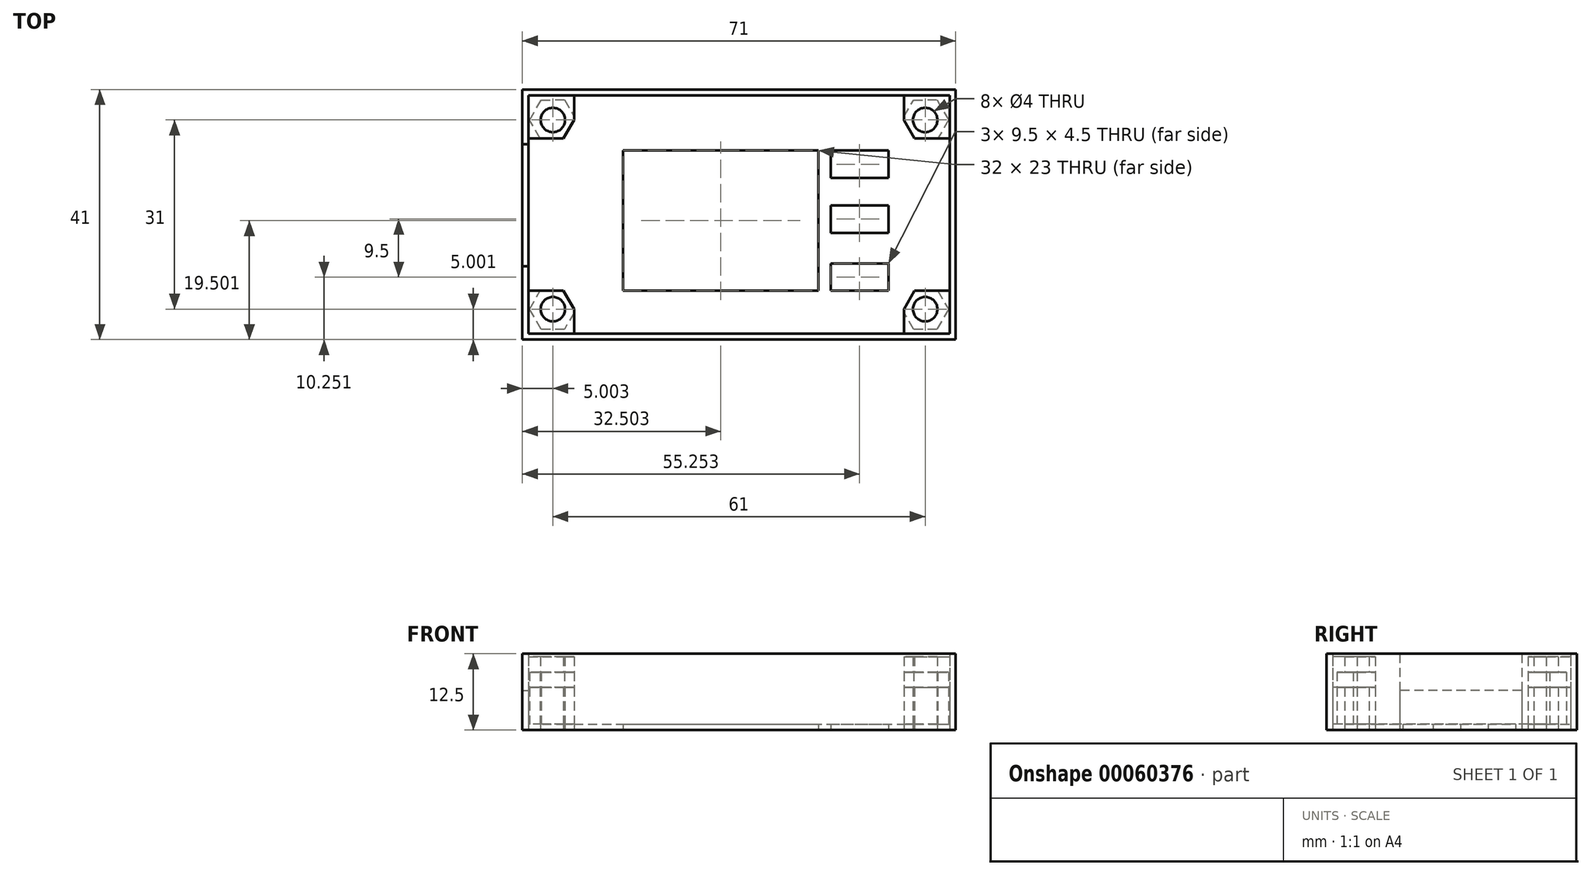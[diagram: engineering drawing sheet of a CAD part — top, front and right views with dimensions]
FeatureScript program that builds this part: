
annotation { "Feature Type Name" : "Feature", "Feature Type Description" : "" }
export const myFeature = defineFeature(function(context is Context, id is Id, definition is map)
    precondition{}
    {
        {
            var Q0;
            Q0=qCreatedBy(makeId("Top.planeOp"),FACE);
            var sketch = newSketch(context, id + "F0", { "sketchPlane" : qUnion([Q0])});
            skCircle(sketch, "E0.cCircle", {"center": v(0, 0) * mm, "radius": 3 * mm, "construction": true});
            skLineSegment(sketch, "E0.0", {"start": v(1.73, 3) * mm, "end": v(3.46, 0) * mm});
            skLineSegment(sketch, "E0.1", {"start": v(3.46, 0) * mm, "end": v(1.74, -3) * mm});
            skLineSegment(sketch, "E0.2", {"start": v(1.74, -3) * mm, "end": v(-1.73, -3) * mm});
            skLineSegment(sketch, "E0.3", {"start": v(-1.73, -3) * mm, "end": v(-3.46, 0) * mm});
            skLineSegment(sketch, "E0.4", {"start": v(-3.46, 0) * mm, "end": v(-1.74, 3) * mm});
            skLineSegment(sketch, "E0.5", {"start": v(-1.74, 3) * mm, "end": v(1.73, 3) * mm});
            skPoint(sketch, "E0.0.midPoint", {"position": v(2.6, 1.5) * mm});
            skCircle(sketch, "E1", {"center": v(0, 0) * mm, "radius": 1.5 * mm});
            skLineSegment(sketch, "E2.bottom", {"start": v(-12.76, 68.41) * mm, "end": v(56.24, 68.41) * mm});
            skLineSegment(sketch, "E2.top", {"start": v(-12.76, 29.41) * mm, "end": v(56.24, 29.41) * mm});
            skLineSegment(sketch, "E2.left", {"start": v(-12.76, 68.41) * mm, "end": v(-12.76, 29.41) * mm});
            skLineSegment(sketch, "E2.right", {"start": v(56.24, 68.41) * mm, "end": v(56.24, 29.41) * mm});
            skPoint(sketch, "E3.0.midPoint", {"position": v(-6.16, 65.92) * mm});
            skLineSegment(sketch, "E3.3", {"start": v(-10.48, 61.4) * mm, "end": v(-12.22, 64.4) * mm, "construction": true});
            skLineSegment(sketch, "E3.2", {"start": v(-7.02, 61.41) * mm, "end": v(-10.48, 61.4) * mm});
            skLineSegment(sketch, "E3.1", {"start": v(-5.3, 64.42) * mm, "end": v(-7.02, 61.41) * mm});
            skLineSegment(sketch, "E3.0", {"start": v(-7.03, 67.41) * mm, "end": v(-5.3, 64.42) * mm, "construction": true});
            skLineSegment(sketch, "E3.4", {"start": v(-12.22, 64.4) * mm, "end": v(-10.5, 67.4) * mm, "construction": true});
            skLineSegment(sketch, "E3.5", {"start": v(-10.5, 67.4) * mm, "end": v(-7.03, 67.41) * mm, "construction": true});
            skCircle(sketch, "E4", {"center": v(-8.76, 64.41) * mm, "radius": 1.5 * mm, "construction": true});
            skCircle(sketch, "E3.cCircle", {"center": v(-8.76, 64.41) * mm, "radius": 3 * mm, "construction": true});
            skPoint(sketch, "E5.0.midPoint", {"position": v(-6.16, 34.92) * mm});
            skLineSegment(sketch, "E5.3", {"start": v(-10.48, 30.4) * mm, "end": v(-12.22, 33.4) * mm, "construction": true});
            skLineSegment(sketch, "E5.2", {"start": v(-7.02, 30.41) * mm, "end": v(-10.48, 30.4) * mm, "construction": true});
            skLineSegment(sketch, "E5.1", {"start": v(-5.3, 33.42) * mm, "end": v(-7.02, 30.41) * mm, "construction": true});
            skLineSegment(sketch, "E5.0", {"start": v(-7.03, 36.41) * mm, "end": v(-5.3, 33.42) * mm});
            skLineSegment(sketch, "E5.4", {"start": v(-12.22, 33.4) * mm, "end": v(-10.5, 36.4) * mm, "construction": true});
            skLineSegment(sketch, "E5.5", {"start": v(-10.5, 36.4) * mm, "end": v(-7.03, 36.41) * mm});
            skCircle(sketch, "E6", {"center": v(-8.76, 33.41) * mm, "radius": 1.5 * mm, "construction": true});
            skCircle(sketch, "E5.cCircle", {"center": v(-8.76, 33.41) * mm, "radius": 3 * mm, "construction": true});
            skPoint(sketch, "E7.0.midPoint", {"position": v(54.84, 65.92) * mm});
            skLineSegment(sketch, "E7.3", {"start": v(50.52, 61.4) * mm, "end": v(48.78, 64.4) * mm});
            skLineSegment(sketch, "E7.2", {"start": v(53.98, 61.41) * mm, "end": v(50.52, 61.4) * mm});
            skLineSegment(sketch, "E7.1", {"start": v(55.7, 64.42) * mm, "end": v(53.98, 61.41) * mm, "construction": true});
            skLineSegment(sketch, "E7.0", {"start": v(53.97, 67.41) * mm, "end": v(55.7, 64.42) * mm, "construction": true});
            skLineSegment(sketch, "E7.4", {"start": v(48.78, 64.4) * mm, "end": v(50.5, 67.4) * mm, "construction": true});
            skLineSegment(sketch, "E7.5", {"start": v(50.5, 67.4) * mm, "end": v(53.97, 67.41) * mm, "construction": true});
            skCircle(sketch, "E8", {"center": v(52.24, 64.41) * mm, "radius": 1.5 * mm, "construction": true});
            skCircle(sketch, "E7.cCircle", {"center": v(52.24, 64.41) * mm, "radius": 3 * mm, "construction": true});
            skPoint(sketch, "E9.0.midPoint", {"position": v(54.84, 34.92) * mm});
            skLineSegment(sketch, "E9.3", {"start": v(50.52, 30.4) * mm, "end": v(48.78, 33.4) * mm, "construction": true});
            skLineSegment(sketch, "E9.2", {"start": v(53.98, 30.41) * mm, "end": v(50.52, 30.4) * mm, "construction": true});
            skLineSegment(sketch, "E9.1", {"start": v(55.7, 33.42) * mm, "end": v(53.98, 30.41) * mm, "construction": true});
            skLineSegment(sketch, "E9.0", {"start": v(53.97, 36.41) * mm, "end": v(55.7, 33.42) * mm, "construction": true});
            skLineSegment(sketch, "E9.4", {"start": v(48.78, 33.4) * mm, "end": v(50.5, 36.4) * mm});
            skLineSegment(sketch, "E9.5", {"start": v(50.5, 36.4) * mm, "end": v(53.97, 36.41) * mm});
            skCircle(sketch, "E10", {"center": v(52.24, 33.41) * mm, "radius": 1.5 * mm, "construction": true});
            skCircle(sketch, "E9.cCircle", {"center": v(52.24, 33.41) * mm, "radius": 3 * mm, "construction": true});
            skLineSegment(sketch, "E11", {"start": v(48.78, 33.4) * mm, "end": v(48.78, 29.41) * mm});
            skLineSegment(sketch, "E12", {"start": v(53.97, 36.41) * mm, "end": v(56.24, 36.41) * mm});
            skCircle(sketch, "E13.0", {"center": v(52.24, 33.41) * mm, "radius": 2 * mm});
            skLineSegment(sketch, "E14.0", {"start": v(50.34, 30.1) * mm, "end": v(48.52, 33.25) * mm});
            skLineSegment(sketch, "E14.1", {"start": v(54.15, 30.11) * mm, "end": v(50.34, 30.1) * mm});
            skLineSegment(sketch, "E14.2", {"start": v(56.05, 33.42) * mm, "end": v(54.15, 30.11) * mm});
            skLineSegment(sketch, "E14.3", {"start": v(54.23, 36.56) * mm, "end": v(56.05, 33.42) * mm});
            skLineSegment(sketch, "E15", {"start": v(-5.3, 33.42) * mm, "end": v(-5.3, 29.41) * mm});
            skLineSegment(sketch, "E16", {"start": v(-10.5, 36.4) * mm, "end": v(-12.76, 36.4) * mm});
            skLineSegment(sketch, "E17", {"start": v(-10.48, 61.4) * mm, "end": v(-12.76, 61.4) * mm});
            skLineSegment(sketch, "E18", {"start": v(-5.3, 64.42) * mm, "end": v(-5.3, 68.41) * mm});
            skLineSegment(sketch, "E19", {"start": v(53.98, 61.41) * mm, "end": v(56.24, 61.42) * mm});
            skLineSegment(sketch, "E20", {"start": v(48.78, 64.4) * mm, "end": v(48.78, 68.41) * mm});
            skCircle(sketch, "E21.0", {"center": v(52.24, 64.41) * mm, "radius": 2 * mm});
            skCircle(sketch, "E22.0", {"center": v(-8.76, 64.41) * mm, "radius": 2 * mm});
            skCircle(sketch, "E23.0", {"center": v(-8.76, 33.41) * mm, "radius": 2 * mm});
            skLineSegment(sketch, "E24.0", {"start": v(-6.86, 67.71) * mm, "end": v(-5.03, 64.57) * mm});
            skLineSegment(sketch, "E24.1", {"start": v(-10.67, 67.7) * mm, "end": v(-6.86, 67.71) * mm});
            skLineSegment(sketch, "E24.2", {"start": v(-12.57, 64.4) * mm, "end": v(-10.67, 67.7) * mm});
            skLineSegment(sketch, "E24.3", {"start": v(-10.74, 61.26) * mm, "end": v(-12.57, 64.4) * mm});
            skLineSegment(sketch, "E25.0", {"start": v(-12.57, 33.4) * mm, "end": v(-10.76, 36.56) * mm});
            skLineSegment(sketch, "E25.1", {"start": v(-10.66, 30.1) * mm, "end": v(-12.57, 33.4) * mm});
            skLineSegment(sketch, "E25.2", {"start": v(-6.85, 30.11) * mm, "end": v(-10.66, 30.1) * mm});
            skLineSegment(sketch, "E25.3", {"start": v(-5.03, 33.27) * mm, "end": v(-6.85, 30.11) * mm});
            skLineSegment(sketch, "E26.0", {"start": v(56.05, 64.42) * mm, "end": v(50.35, 54.5) * mm});
            skLineSegment(sketch, "E26.1", {"start": v(54.14, 67.71) * mm, "end": v(56.05, 64.42) * mm});
            skLineSegment(sketch, "E26.2", {"start": v(50.33, 67.7) * mm, "end": v(54.14, 67.71) * mm});
            skLineSegment(sketch, "E26.3", {"start": v(48.52, 64.55) * mm, "end": v(50.33, 67.7) * mm});
            skPoint(sketch, "E27", {"position": v(2.74, 36.41) * mm});
            skLineSegment(sketch, "E28.bottom", {"start": v(2.74, 36.41) * mm, "end": v(34.74, 36.41) * mm});
            skLineSegment(sketch, "E28.top", {"start": v(2.74, 59.41) * mm, "end": v(34.74, 59.41) * mm});
            skLineSegment(sketch, "E28.left", {"start": v(2.74, 36.41) * mm, "end": v(2.74, 59.41) * mm});
            skLineSegment(sketch, "E28.right", {"start": v(34.74, 36.41) * mm, "end": v(34.74, 59.41) * mm});
            skPoint(sketch, "E29", {"position": v(36.74, 59.41) * mm});
            skLineSegment(sketch, "E30.bottom", {"start": v(36.74, 59.41) * mm, "end": v(46.24, 59.41) * mm});
            skLineSegment(sketch, "E30.top", {"start": v(36.74, 54.91) * mm, "end": v(46.24, 54.91) * mm});
            skLineSegment(sketch, "E30.left", {"start": v(36.74, 59.41) * mm, "end": v(36.74, 54.91) * mm});
            skLineSegment(sketch, "E30.right", {"start": v(46.24, 59.41) * mm, "end": v(46.24, 54.91) * mm});
            skLineSegment(sketch, "E31.bottom", {"start": v(36.74, 36.41) * mm, "end": v(46.24, 36.41) * mm});
            skLineSegment(sketch, "E31.top", {"start": v(36.74, 40.91) * mm, "end": v(46.24, 40.91) * mm});
            skLineSegment(sketch, "E31.left", {"start": v(36.74, 36.41) * mm, "end": v(36.74, 40.91) * mm});
            skLineSegment(sketch, "E31.right", {"start": v(46.24, 36.41) * mm, "end": v(46.24, 40.91) * mm});
            skLineSegment(sketch, "E32.bottom", {"start": v(36.74, 45.91) * mm, "end": v(46.24, 45.91) * mm});
            skLineSegment(sketch, "E32.top", {"start": v(36.74, 50.41) * mm, "end": v(46.24, 50.41) * mm});
            skLineSegment(sketch, "E32.left", {"start": v(36.74, 45.91) * mm, "end": v(36.74, 50.41) * mm});
            skLineSegment(sketch, "E32.right", {"start": v(46.24, 45.91) * mm, "end": v(46.24, 50.41) * mm});
            skLineSegment(sketch, "E33.0", {"start": v(-13.76, 69.41) * mm, "end": v(-13.76, 28.41) * mm});
            skLineSegment(sketch, "E33.1", {"start": v(-13.76, 69.41) * mm, "end": v(57.24, 69.41) * mm});
            skLineSegment(sketch, "E33.2", {"start": v(57.24, 69.41) * mm, "end": v(57.24, 28.41) * mm});
            skLineSegment(sketch, "E33.3", {"start": v(-13.76, 28.41) * mm, "end": v(57.24, 28.41) * mm});
            skPoint(sketch, "E34", {"position": v(-13.76, 60.41) * mm});
            skPoint(sketch, "E35", {"position": v(-13.76, 40.41) * mm});
            skLineSegment(sketch, "E36", {"start": v(-13.76, 60.41) * mm, "end": v(-12.76, 60.41) * mm});
            skLineSegment(sketch, "E37", {"start": v(-13.76, 40.41) * mm, "end": v(-12.76, 40.41) * mm});
            skSolve(sketch);
        }
        {
            var Q0;
            {var subQ12=sQuery(id+"F0.wireOp",EDGE,"E14.1");Q0=makeQuery(id+"F0.imprint","IMPRINT",FACE,{"disambiguationData":[TD([[makeQuery(id+"F0.imprint","IMPRINT",EDGE,{"derivedFrom":subQ12}),1.0]])]});}
            var Q1;
            {var subQ6=sQuery(id+"F0.wireOp",EDGE,"E9.4");Q1=makeQuery(id+"F0.imprint","IMPRINT",FACE,{"disambiguationData":[TD([[makeQuery(id+"F0.imprint","IMPRINT",EDGE,{"derivedFrom":subQ6}),-1.0]])]});}
            var Q2;
            {var subQ5=sQuery(id+"F0.wireOp",EDGE,"E25.1");Q2=makeQuery(id+"F0.imprint","IMPRINT",FACE,{"disambiguationData":[TD([[makeQuery(id+"F0.imprint","IMPRINT",EDGE,{"derivedFrom":subQ5}),1.0]])]});}
            var Q3;
            {var subQ5=sQuery(id+"F0.wireOp",EDGE,"E5.0");Q3=makeQuery(id+"F0.imprint","IMPRINT",FACE,{"disambiguationData":[TD([[makeQuery(id+"F0.imprint","IMPRINT",EDGE,{"derivedFrom":subQ5}),-1.0]])]});}
            var Q4;
            {var subQ11=sQuery(id+"F0.wireOp",EDGE,"E24.1");Q4=makeQuery(id+"F0.imprint","IMPRINT",FACE,{"disambiguationData":[TD([[makeQuery(id+"F0.imprint","IMPRINT",EDGE,{"derivedFrom":subQ11}),1.0]])]});}
            var Q5;
            {var subQ5=sQuery(id+"F0.wireOp",EDGE,"E3.2");Q5=makeQuery(id+"F0.imprint","IMPRINT",FACE,{"disambiguationData":[TD([[makeQuery(id+"F0.imprint","IMPRINT",EDGE,{"derivedFrom":subQ5}),-1.0]])]});}
            var Q6;
            {var subQ7=sQuery(id+"F0.wireOp",EDGE,"E26.1");Q6=makeQuery(id+"F0.imprint","IMPRINT",FACE,{"disambiguationData":[TD([[makeQuery(id+"F0.imprint","IMPRINT",EDGE,{"derivedFrom":subQ7}),1.0]])]});}
            var Q7;
            {var subQ1=sQuery(id+"F0.wireOp",EDGE,"E7.3");Q7=makeQuery(id+"F0.imprint","IMPRINT",FACE,{"disambiguationData":[TD([[makeQuery(id+"F0.imprint","IMPRINT",EDGE,{"derivedFrom":subQ1}),-1.0]])]});}
            extrude(context, id + "F1", {"entities" : qUnion([Q0, Q1, Q2, Q3, Q4, Q5, Q6, Q7]), "depth" : 7 * mm});
        }
        {
            var Q0;
            {var subQ12=sQuery(id+"F0.wireOp",EDGE,"E14.1");Q0=makeQuery(id+"F0.imprint","IMPRINT",FACE,{"disambiguationData":[TD([[makeQuery(id+"F0.imprint","IMPRINT",EDGE,{"derivedFrom":subQ12}),1.0]])]});}
            var Q1;
            {var subQ7=sQuery(id+"F0.wireOp",EDGE,"E26.1");Q1=makeQuery(id+"F0.imprint","IMPRINT",FACE,{"disambiguationData":[TD([[makeQuery(id+"F0.imprint","IMPRINT",EDGE,{"derivedFrom":subQ7}),1.0]])]});}
            var Q2;
            {var subQ11=sQuery(id+"F0.wireOp",EDGE,"E24.1");Q2=makeQuery(id+"F0.imprint","IMPRINT",FACE,{"disambiguationData":[TD([[makeQuery(id+"F0.imprint","IMPRINT",EDGE,{"derivedFrom":subQ11}),1.0]])]});}
            var Q3;
            {var subQ5=sQuery(id+"F0.wireOp",EDGE,"E25.1");Q3=makeQuery(id+"F0.imprint","IMPRINT",FACE,{"disambiguationData":[TD([[makeQuery(id+"F0.imprint","IMPRINT",EDGE,{"derivedFrom":subQ5}),1.0]])]});}
            extrude(context, id + "F2", {"entities" : qUnion([Q0, Q1, Q2, Q3]), "endBound" : BoundingType.UP_TO_NEXT, "depth" : 25 * mm});
        }
        {
            var Q0;
            Q0=makeQuery(id+"F2.opExtrude","CAP_FACE",FACE,{"disambiguationData":[OSD([sQuery(id+"F0.wireOp",EDGE,"E2.top"),sQuery(id+"F0.wireOp",EDGE,"E2.right"),sQuery(id+"F0.wireOp",EDGE,"E9.4"),sQuery(id+"F0.wireOp",EDGE,"E9.5"),sQuery(id+"F0.wireOp",EDGE,"E11"),sQuery(id+"F0.wireOp",EDGE,"E12"),sQuery(id+"F0.wireOp",EDGE,"E13.0")])],"isStart":false});
            var Q1;
            Q1=makeQuery(id+"F2.opExtrude","CAP_FACE",FACE,{"disambiguationData":[OSD([sQuery(id+"F0.wireOp",EDGE,"E2.top"),sQuery(id+"F0.wireOp",EDGE,"E2.left"),sQuery(id+"F0.wireOp",EDGE,"E5.0"),sQuery(id+"F0.wireOp",EDGE,"E5.5"),sQuery(id+"F0.wireOp",EDGE,"E15"),sQuery(id+"F0.wireOp",EDGE,"E16"),sQuery(id+"F0.wireOp",EDGE,"E23.0")])],"isStart":false});
            var Q2;
            Q2=makeQuery(id+"F2.opExtrude","CAP_FACE",FACE,{"disambiguationData":[OSD([sQuery(id+"F0.wireOp",EDGE,"E2.bottom"),sQuery(id+"F0.wireOp",EDGE,"E2.left"),sQuery(id+"F0.wireOp",EDGE,"E3.2"),sQuery(id+"F0.wireOp",EDGE,"E3.1"),sQuery(id+"F0.wireOp",EDGE,"E17"),sQuery(id+"F0.wireOp",EDGE,"E18"),sQuery(id+"F0.wireOp",EDGE,"E22.0")])],"isStart":false});
            var Q3;
            Q3=makeQuery(id+"F2.opExtrude","CAP_FACE",FACE,{"disambiguationData":[OSD([sQuery(id+"F0.wireOp",EDGE,"E2.bottom"),sQuery(id+"F0.wireOp",EDGE,"E2.right"),sQuery(id+"F0.wireOp",EDGE,"E7.3"),sQuery(id+"F0.wireOp",EDGE,"E7.2"),sQuery(id+"F0.wireOp",EDGE,"E19"),sQuery(id+"F0.wireOp",EDGE,"E20"),sQuery(id+"F0.wireOp",EDGE,"E21.0")])],"isStart":false});
            extrude(context, id + "F3", {"entities" : qUnion([Q0, Q1, Q2, Q3]), "depth" : 2.5 * mm});
        }
        {
            var Q0;
            Q0=makeQuery(id+"F1.opExtrude","CAP_FACE",FACE,{"disambiguationData":[OSD([sQuery(id+"F0.wireOp",EDGE,"E2.top"),sQuery(id+"F0.wireOp",EDGE,"E2.right"),sQuery(id+"F0.wireOp",EDGE,"E9.4"),sQuery(id+"F0.wireOp",EDGE,"E9.5"),sQuery(id+"F0.wireOp",EDGE,"E11"),sQuery(id+"F0.wireOp",EDGE,"E12"),sQuery(id+"F0.wireOp",EDGE,"E13.0")])],"isStart":false});
            var Q1;
            Q1=makeQuery(id+"F1.opExtrude","CAP_FACE",FACE,{"disambiguationData":[OSD([sQuery(id+"F0.wireOp",EDGE,"E2.top"),sQuery(id+"F0.wireOp",EDGE,"E2.left"),sQuery(id+"F0.wireOp",EDGE,"E5.0"),sQuery(id+"F0.wireOp",EDGE,"E5.5"),sQuery(id+"F0.wireOp",EDGE,"E15"),sQuery(id+"F0.wireOp",EDGE,"E16"),sQuery(id+"F0.wireOp",EDGE,"E23.0")])],"isStart":false});
            var Q2;
            Q2=makeQuery(id+"F1.opExtrude","CAP_FACE",FACE,{"disambiguationData":[OSD([sQuery(id+"F0.wireOp",EDGE,"E2.bottom"),sQuery(id+"F0.wireOp",EDGE,"E2.left"),sQuery(id+"F0.wireOp",EDGE,"E3.2"),sQuery(id+"F0.wireOp",EDGE,"E3.1"),sQuery(id+"F0.wireOp",EDGE,"E17"),sQuery(id+"F0.wireOp",EDGE,"E18"),sQuery(id+"F0.wireOp",EDGE,"E22.0")])],"isStart":false});
            var Q3;
            Q3=makeQuery(id+"F1.opExtrude","CAP_FACE",FACE,{"disambiguationData":[OSD([sQuery(id+"F0.wireOp",EDGE,"E2.bottom"),sQuery(id+"F0.wireOp",EDGE,"E2.right"),sQuery(id+"F0.wireOp",EDGE,"E7.3"),sQuery(id+"F0.wireOp",EDGE,"E7.2"),sQuery(id+"F0.wireOp",EDGE,"E19"),sQuery(id+"F0.wireOp",EDGE,"E20"),sQuery(id+"F0.wireOp",EDGE,"E21.0")])],"isStart":false});
            extrude(context, id + "F4", {"entities" : qUnion([Q0, Q1, Q2, Q3]), "operationType" : NewBodyOperationType.ADD, "depth" : 5 * mm, "hasSecondDirection" : true, "secondDirectionOppositeDirection" : false, "secondDirectionDepth" : 2.5 * mm});
        }
        {
            var Q0;
            {var subQ14=sQuery(id+"F0.wireOp",EDGE,"E3.2");Q0=makeQuery(id+"F0.imprint","IMPRINT",FACE,{"disambiguationData":[TD([[makeQuery(id+"F0.imprint","IMPRINT",EDGE,{"derivedFrom":subQ14}),1.0]])]});}
            var Q1;
            Q1=makeQuery(id+"F0.imprint","IMPRINT",FACE,{"disambiguationData":[TD([[makeQuery(id+"F0.imprint","IMPRINT",EDGE,{"derivedFrom":sQuery(id+"F0.wireOp",EDGE,"E22.0")}),1.0]])]});
            var Q2;
            Q2=makeQuery(id+"F0.imprint","IMPRINT",FACE,{"disambiguationData":[TD([[makeQuery(id+"F0.imprint","IMPRINT",EDGE,{"derivedFrom":sQuery(id+"F0.wireOp",EDGE,"E21.0")}),1.0]])]});
            var Q3;
            Q3=makeQuery(id+"F0.imprint","IMPRINT",FACE,{"disambiguationData":[TD([[makeQuery(id+"F0.imprint","IMPRINT",EDGE,{"derivedFrom":sQuery(id+"F0.wireOp",EDGE,"E13.0")}),1.0]])]});
            var Q4;
            Q4=makeQuery(id+"F0.imprint","IMPRINT",FACE,{"disambiguationData":[TD([[makeQuery(id+"F0.imprint","IMPRINT",EDGE,{"derivedFrom":sQuery(id+"F0.wireOp",EDGE,"E23.0")}),1.0]])]});
            extrude(context, id + "F5", {"entities" : qUnion([Q0, Q1, Q2, Q3, Q4]), "depth" : 1 * mm});
        }
        {
            var Q0;
            {var subQ18=sQuery(id+"F0.wireOp",EDGE,"E33.1");Q0=makeQuery(id+"F0.imprint","IMPRINT",FACE,{"disambiguationData":[TD([[makeQuery(id+"F0.imprint","IMPRINT",EDGE,{"derivedFrom":subQ18}),-1.0]])]});}
            extrude(context, id + "F6", {"entities" : qUnion([Q0]), "depth" : 12.5 * mm});
        }
        {
            var Q0;
            {var subQ0=sQuery(id+"F0.wireOp",EDGE,"E36");Q0=makeQuery(id+"F0.imprint","IMPRINT",FACE,{"disambiguationData":[TD([[makeQuery(id+"F0.imprint","IMPRINT",EDGE,{"derivedFrom":subQ0}),-1.0]])]});}
            extrude(context, id + "F7", {"entities" : qUnion([Q0]), "depth" : 6.5 * mm});
        }
    });
